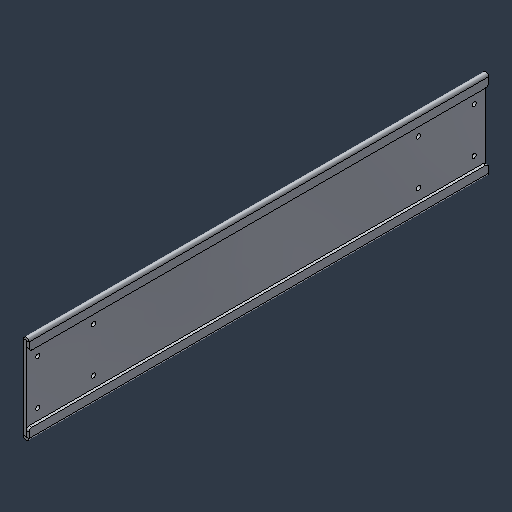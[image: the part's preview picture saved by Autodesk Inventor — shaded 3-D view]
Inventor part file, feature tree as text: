
AUTODESK INVENTOR PART (.ipt)
format: ipt  version: 2024.3 (Build 283343000, 343)  size: 111,616 bytes
history: native  units: mm (DEFAULTED — no unit token found)
features: fillet x1
ambient origin geometry x8: Origin, YZ Plane, XZ Plane, XY Plane, X Axis, Y Axis, Z Axis, Center Point
bodies: Solid1 (feature_tree)
feature tree (1):
  fillet  "Fillet1"  [1 undecoded]
note: 1 required parameter value undecoded (feature->parameter linkage not recoverable at this tier; creation-order binding heuristic only, values carry confidence <= 0.55)
